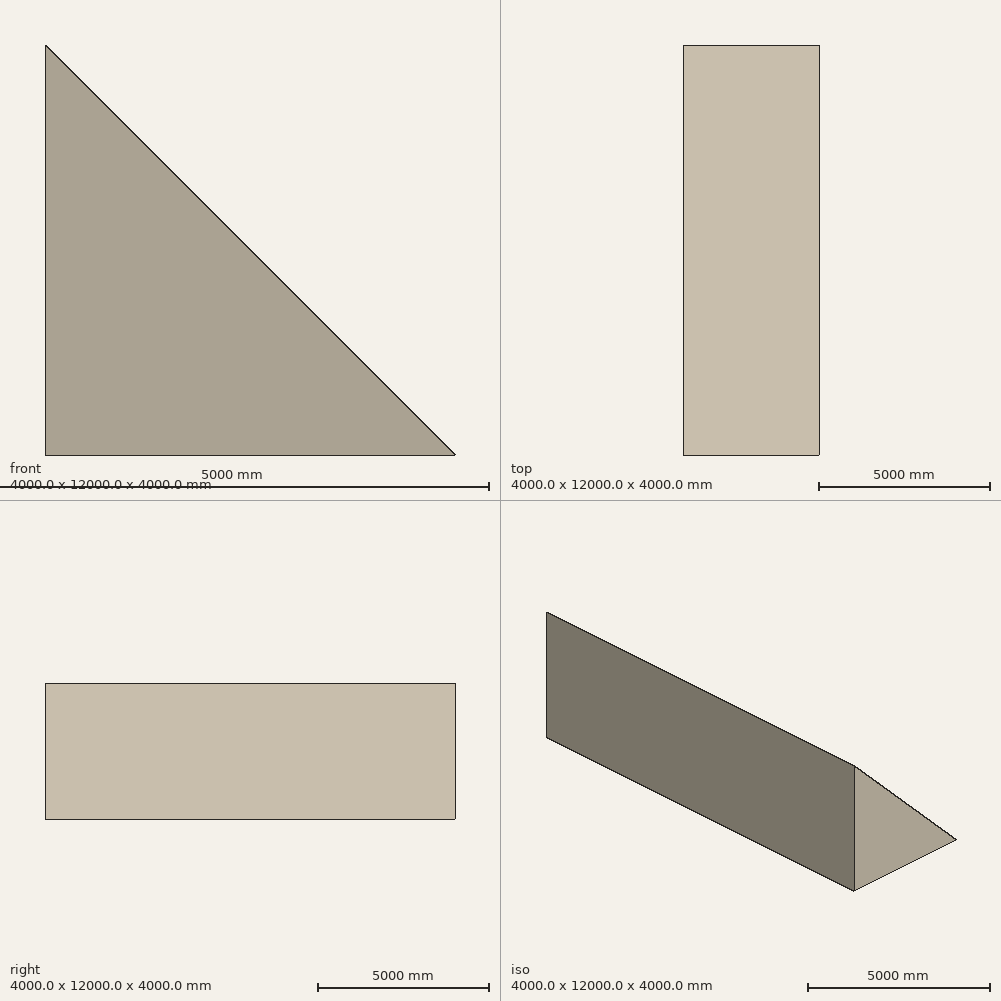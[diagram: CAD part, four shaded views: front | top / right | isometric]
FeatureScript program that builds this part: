
annotation { "Feature Type Name" : "Feature", "Feature Type Description" : "" }
export const myFeature = defineFeature(function(context is Context, id is Id, definition is map)
    precondition{}
    {
        {
            var Q0;
            Q0=qCreatedBy(makeId("Front.planeOp"),FACE);
            var sketch = newSketch(context, id + "F0", { "sketchPlane" : qUnion([Q0])});
            skLineSegment(sketch, "E0", {"start": v(0, 0) * mm, "end": v(0, 4000) * mm});
            skLineSegment(sketch, "E1", {"start": v(0, 4000) * mm, "end": v(4000, 0) * mm});
            skLineSegment(sketch, "E2", {"start": v(4000, 0) * mm, "end": v(0, 0) * mm});
            skSolve(sketch);
        }
        {
            var Q0;
            Q0 = qSketchRegion(id + "F0", true);
            extrude(context, id + "F1", {"entities" : qUnion([Q0]), "depth" : 12000 * mm});
        }
    });
